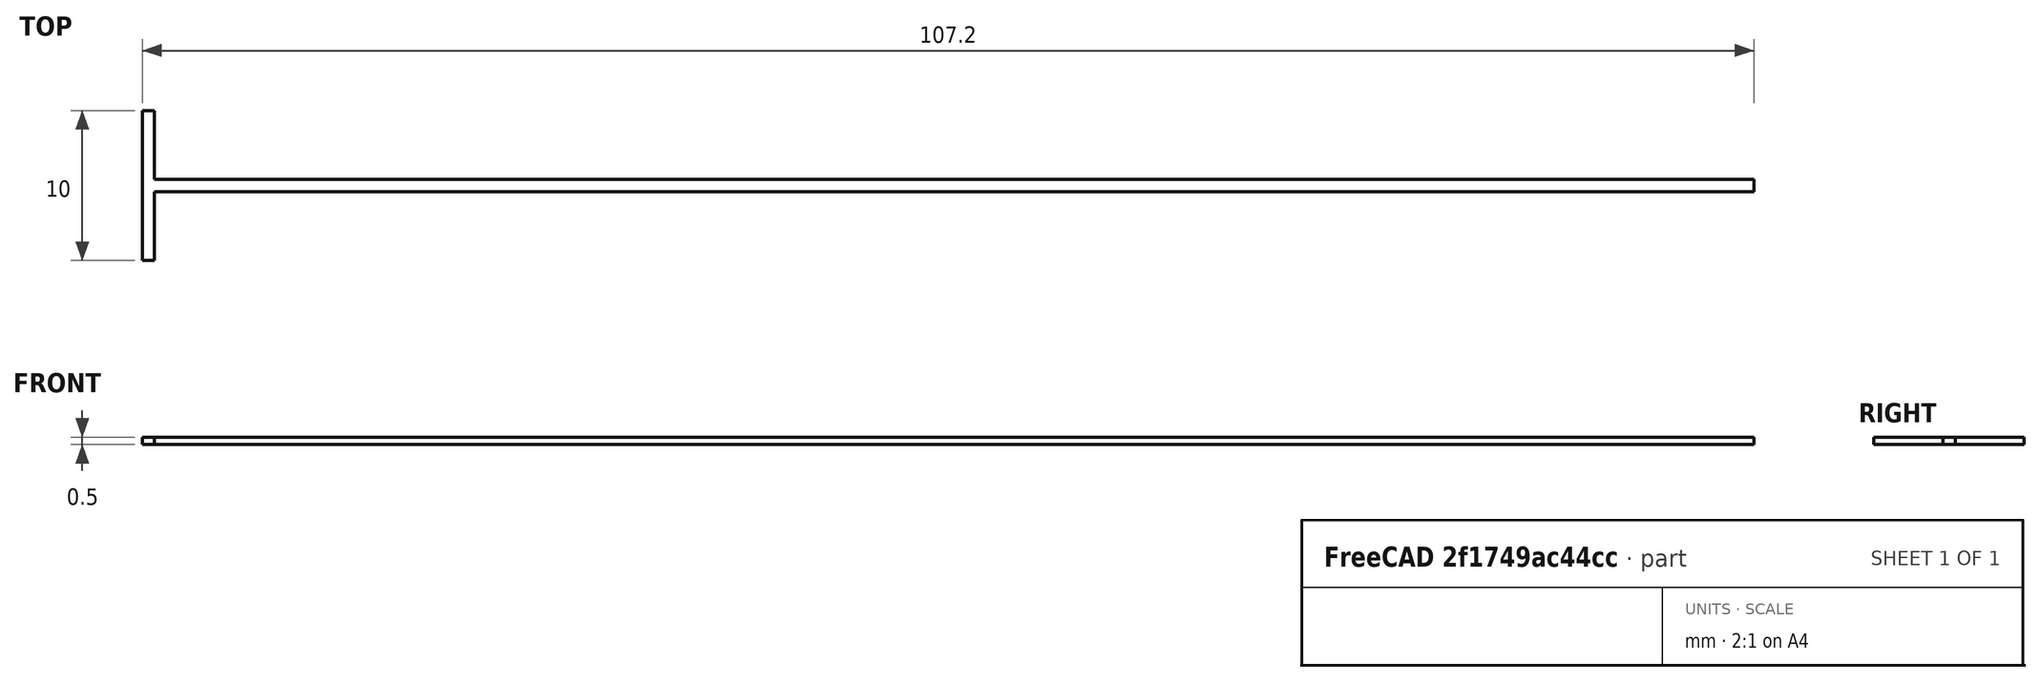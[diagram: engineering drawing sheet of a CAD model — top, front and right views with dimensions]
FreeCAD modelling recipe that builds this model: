
FCSTD DOCUMENT  (FreeCAD 0.20R29177 (Git))
Label: ax1_and_vein
License: All rights reserved
LicenseURL: http://en.wikipedia.org/wiki/All_rights_reserved
objects: Spreadsheet::Sheet×1, Sketcher::SketchObject×1, PartDesign::Pad×1, PartDesign::Body×1
note: 4 computed .brp shape members not serialized (recipe doc carries the construction recipe); baked Part::Feature solids carry a one-line shape summary decoded from their .brp

FEATURE [Spreadsheet::Sheet] Spreadsheet
  cells = A2=Design Parameters; A3=RefLength; B3(RefLength)==1mm; A4=Width; B4(Width)==0.8 * RefLength; A5=Height; B5(Height)==0.5 * RefLength; A6=PwpToTipLength; B6(PwpToTipLength)==100 * RefLength; A7=MuAngle; B7(MuAngle)==20deg; A8=MuAxisToBallCenter; B8(MuAxisToBallCenter)==5.25 * RefLength; A9=MuAdjustedLength; B9(MuAdjustedLength)==MuAxisToBallCenter * sin(MuAngle); A10=PwpToBaseLength; B10(PwpToBaseLength)==5 * RefLength + MuAdjustedLength; A11=SlaOffset; B11(SlaOffset)==5 * RefLength; A12=ScuOffset; B12(ScuOffset)==5 * RefLength
FEATURE [Sketcher::SketchObject] Sketch
  FullyConstrained = true
  MapMode = 5
  Support = -> [XY_Plane]
  expr: Constraints[17] = Spreadsheet.ScuOffset
  expr: Constraints[18] = Spreadsheet.SlaOffset
  expr: Constraints[19] = Spreadsheet.Width
  expr: Constraints[21] = Spreadsheet.Width
  expr: Constraints[41] = Spreadsheet.PwpToBaseLength
  sketch-geometry (17):
    g0: LineSegment StartX=-7.19561 StartY=5 StartZ=0 EndX=-7.19561 EndY=0 EndZ=0
    g1: LineSegment StartX=-7.19561 StartY=0 StartZ=0 EndX=-7.19561 EndY=-5 EndZ=0
    g2: LineSegment StartX=-6.39561 StartY=-5 StartZ=0 EndX=-6.39561 EndY=-0.4 EndZ=0
    g3: LineSegment StartX=-6.39561 StartY=-0.4 StartZ=0 EndX=3.1771e-11 EndY=-0.4 EndZ=0
    g4: LineSegment StartX=3.17708e-11 StartY=-0.4 StartZ=0 EndX=100 EndY=-0.4 EndZ=0
    g5: LineSegment StartX=100 StartY=-0.4 StartZ=0 EndX=100 EndY=0.4 EndZ=0
    g6: LineSegment StartX=100 StartY=0.4 StartZ=0 EndX=0 EndY=0.4 EndZ=0
    g7: LineSegment StartX=0 StartY=0.4 StartZ=0 EndX=-6.39561 EndY=0.4 EndZ=0
    g8: LineSegment StartX=-6.39561 StartY=0.4 StartZ=0 EndX=-6.39561 EndY=5 EndZ=0
    g9: LineSegment StartX=-7.19561 StartY=5 StartZ=0 EndX=-6.79561 EndY=5 EndZ=0
    g10: LineSegment StartX=-6.79561 StartY=5 StartZ=0 EndX=-6.39561 EndY=5 EndZ=0
    g11: LineSegment StartX=-7.19561 StartY=-5 StartZ=0 EndX=-6.79561 EndY=-5 EndZ=0
    g12: LineSegment StartX=-6.79561 StartY=-5 StartZ=0 EndX=-6.39561 EndY=-5 EndZ=0
    g13: LineSegment StartX=-6.79561 StartY=5 StartZ=0 EndX=-6.79561 EndY=0 EndZ=0
    g14: LineSegment StartX=-6.79561 StartY=0 StartZ=0 EndX=-6.79561 EndY=-5 EndZ=0
    g15: LineSegment StartX=0 StartY=0.4 StartZ=0 EndX=0 EndY=0 EndZ=0
    g16: LineSegment StartX=0 StartY=0 StartZ=0 EndX=3.17708e-11 EndY=-0.4 EndZ=0
  constraints (48):
    c: Vertical(g0)
    c: Coincident(g0,g1)
    c: Vertical(g1)
    c: Vertical(g2)
    c: Coincident(g2,g3)
    c: Horizontal(g3)
    c: Coincident(g3,g4)
    c: Horizontal(g4)
    c: Coincident(g4,g5)
    c: Coincident(g5,g6)
    c: Horizontal(g6)
    c: Coincident(g6,g7)
    c: Horizontal(g7)
    c: Coincident(g7,g8)
    c: Vertical(g8)
    c: Equal(g3,g7)
    c: PointOnObject(g0,g-1)
    c: DistanceY(g0,g0) = 5
    c: DistanceY(g1,g0) = 5
    c: DistanceX(g0,g8) = 0.8
    c: Vertical(g5)
    c: DistanceY(g5,g5) = 0.8
    c: DistanceX(g4,g4) = 100
    c: Horizontal(g9)
    c: Coincident(g9,g10)
    c: Horizontal(g10)
    c: Equal(g9,g10)
    c: Coincident(g0,g9)
    c: Coincident(g10,g8)
    c: Horizontal(g11)
    c: Coincident(g11,g12)
    c: Horizontal(g12)
    c: Equal(g11,g12)
    c: Coincident(g1,g11)
    c: Coincident(g12,g2)
    c: Coincident(g13,g14)
    c: PointOnObject(g13,g-1)
    c: Coincident(g13,g9)
    c: Coincident(g14,g11)
    c: Vertical(g13)
    c: Equal(g9,g11)
    c: DistanceX(g13,g-1) = 6.79561
    c: Coincident(g15,g16)
    c: Equal(g15,g16)
    c: Coincident(g15,g-1)
    c: Coincident(g15,g6)
    c: Coincident(g16,g3)
    c: Vertical(g15)
FEATURE [PartDesign::Pad] Pad
  Direction = (0,0,1)
  Length = 0.5
  Length2 = 10
  Profile = -> Sketch
  ReferenceAxis = -> Sketch [N_Axis]
  Type = 0
  expr: Length = Spreadsheet.Height
FEATURE [PartDesign::Body] Body
  Group = -> [Sketch,Pad]
  Origin = -> Origin
  Tip = -> Pad
